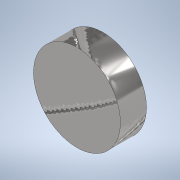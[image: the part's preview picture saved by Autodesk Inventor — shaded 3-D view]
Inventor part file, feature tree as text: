
AUTODESK INVENTOR PART (.ipt)
format: ipt  version: 2020 (Build 240168000, 168)  size: 99,328 bytes
history: native  units: mm
features: extrude x1, sketch x1
ambient origin geometry x8: Origin, YZ Plane, XZ Plane, XY Plane, X Axis, Y Axis, Z Axis, Center Point
bodies: Solid1 (feature_tree)
feature tree (2):
  extrude  "Extrusion1"  Depth=3.0mm TaperAngle=0.0deg
  sketch  "Sketch1"  dims[d0=10.0mm d1=3.0mm d2=0.0mm]
